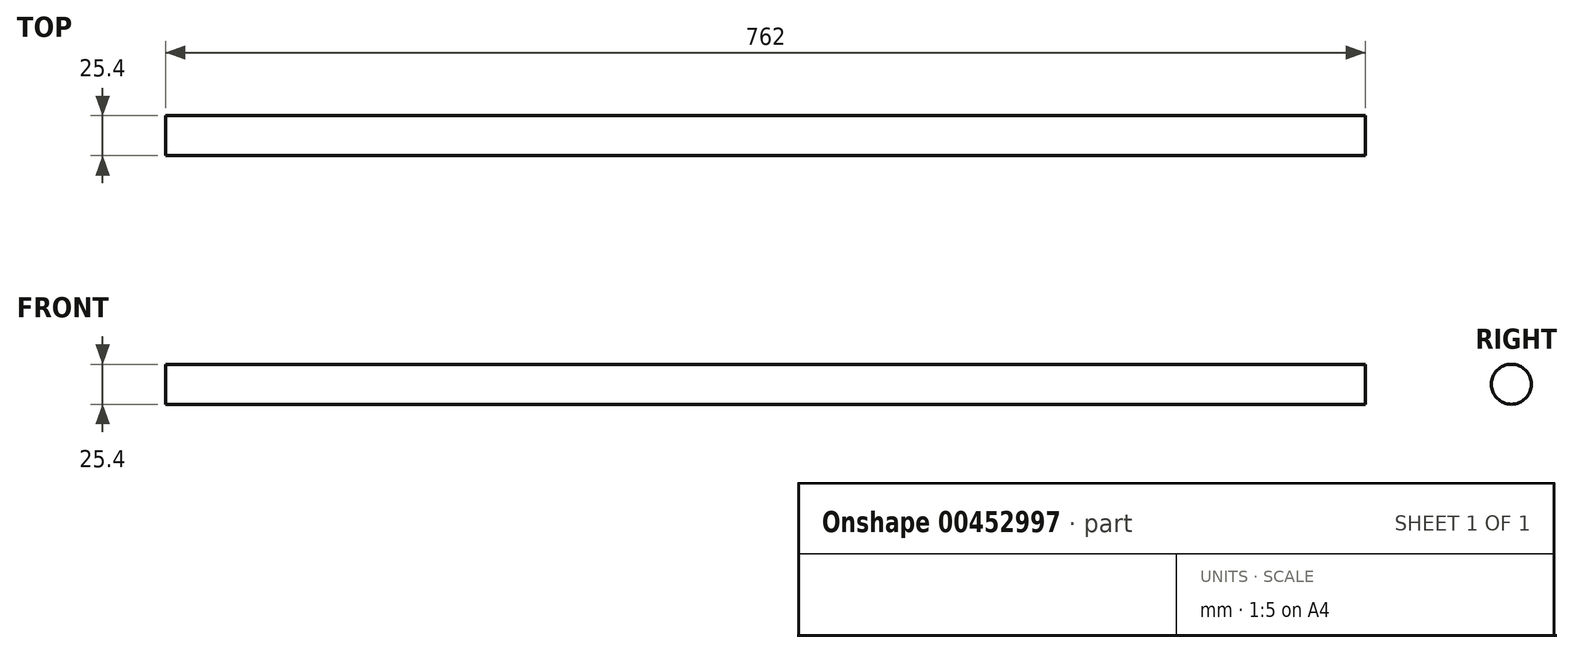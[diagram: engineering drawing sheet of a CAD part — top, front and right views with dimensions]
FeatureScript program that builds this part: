
annotation { "Feature Type Name" : "Feature", "Feature Type Description" : "" }
export const myFeature = defineFeature(function(context is Context, id is Id, definition is map)
    precondition{}
    {
        {
            var Q0;
            Q0=qCreatedBy(makeId("Front.planeOp"),FACE);
            var sketch = newSketch(context, id + "F0", { "sketchPlane" : qUnion([Q0])});
            skLineSegment(sketch, "E0", {"start": v(-377.17, 0) * mm, "end": v(384.83, 0) * mm});
            skPoint(sketch, "E1", {"position": v(-341.64, 0) * mm});
            skPoint(sketch, "E2.MirrorP", {"position": v(341.64, 0) * mm});
            skLineSegment(sketch, "E3", {"start": v(-377.17, 0) * mm, "end": v(-377.17, 12.7) * mm});
            skLineSegment(sketch, "E4", {"start": v(-377.17, 12.7) * mm, "end": v(384.83, 12.7) * mm});
            skLineSegment(sketch, "E5", {"start": v(384.83, 12.7) * mm, "end": v(384.83, 0) * mm});
            skSolve(sketch);
        }
        {
            var Q0;
            Q0=makeQuery(id+"F0.imprint","IMPRINT",FACE,{"disambiguationData":[TD([[makeQuery(id+"F0.imprint","IMPRINT",EDGE,{"derivedFrom":sQuery(id+"F0.wireOp",EDGE,"E0")}),1.0]])]});
            var Q1;
            Q1=sQuery(id+"F0.wireOp",EDGE,"E4");
            revolve(context, id + "F1", {"entities" : qUnion([Q0]), "axis" : qUnion([Q1]), "revolveType" : RevolveType.FULL});
        }
    });
